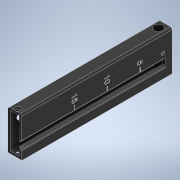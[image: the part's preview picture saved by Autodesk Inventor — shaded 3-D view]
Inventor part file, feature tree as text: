
AUTODESK INVENTOR PART (.ipt)
format: ipt  version: 2021 (Build 250183000, 183)  size: 353,792 bytes
history: native  units: mm
features: sketch x8, extrude x7, chamfer x3, plane x2, revolve x1, fillet x1, mirror x1, pattern_linear x1
ambient origin geometry x8: Origin, YZ Plane, XZ Plane, XY Plane, X Axis, Y Axis, Z Axis, Center Point
bodies: Solid1 (feature_tree)
feature tree (24):
  extrude  "Extrusion1"  Depth=45.0mm
  extrude  "Extrusion2"  Depth=22.5mm
  chamfer  "Chamfer1"  Distance=170.0mm
  plane  "Work Plane1"
  revolve  "Revolution1"  [1 undecoded]
  fillet  "Fillet1"  [1 undecoded]
  mirror  "Mirror1"
  plane  "Work Plane2"
  sketch  "Sketch4"  dims[d10=1.0mm d11=2.0mm d12=45.0deg d13=-20.1mm]
  extrude  "Extrusion3"  [1 undecoded]
  extrude  "Extrusion4"  Depth=3.0mm
  extrude  "Extrusion5"  Depth=2.5mm
  pattern_linear  "Rectangular Pattern1"  Count1=4  [1 undecoded]
  extrude  "Extrusion6"  Depth=10.0mm
  chamfer  "Chamfer2"  [1 undecoded]
  extrude  "Extrusion7"  Depth=5.0mm TaperAngle=0.0deg
  chamfer  "Chamfer3"  Distance=3.2mm
  sketch  "Sketch1"  dims[d0=45.0mm d1=16.0mm]
  sketch  "Sketch2"  dims[d2=1.8mm d3=22.5mm d4=170.0mm d5=0.0mm]
  sketch  "Sketch3"  dims[d6=7.75mm d7=10.0mm d8=0.0mm d9=0.0mm]
  sketch  "Sketch5"  dims[d14=0.75mm d15=3.0mm]
  sketch  "Sketch6"  dims[d16=2.5mm d17=3.0mm]
  sketch  "Sketch7"  dims[d18=90.0deg]
  sketch  "Sketch8"  dims[d19=1.0mm d20=40.0mm d21=10.0mm d22=-7.75mm d23=170.0mm d24=0.0mm d25=3.2mm d26=3.4mm d27=0.0mm d28=0.0mm d29=20.0mm d30=20.0mm d31=6.0mm d32=20.0mm d33=170.0mm d34=0.0mm d35=70.0mm d37=20.0mm d38=5.0mm d39=10.0mm d40=1.5mm d41=170.0mm d42=0.0mm d43=0.5mm d44=2.0mm d45=45.0deg d47=8.0mm d48=36.5mm d49=1.0mm d50=5.0mm d51=8.0mm d52=5.0mm d53=2.0mm d54=8.0mm d55=5.0mm d56=2.0mm d57=73.5mm d58=8.0mm d59=5.0mm d60=8.0mm d61=2.0mm d62=110.5mm d63=37.0mm d64=37.0mm d65=0.2mm d66=0.0mm d67=1.8mm d68=2.0mm d69=45.0deg]
note: 5 required parameter values undecoded (feature->parameter linkage not recoverable at this tier; creation-order binding heuristic only, values carry confidence <= 0.55)